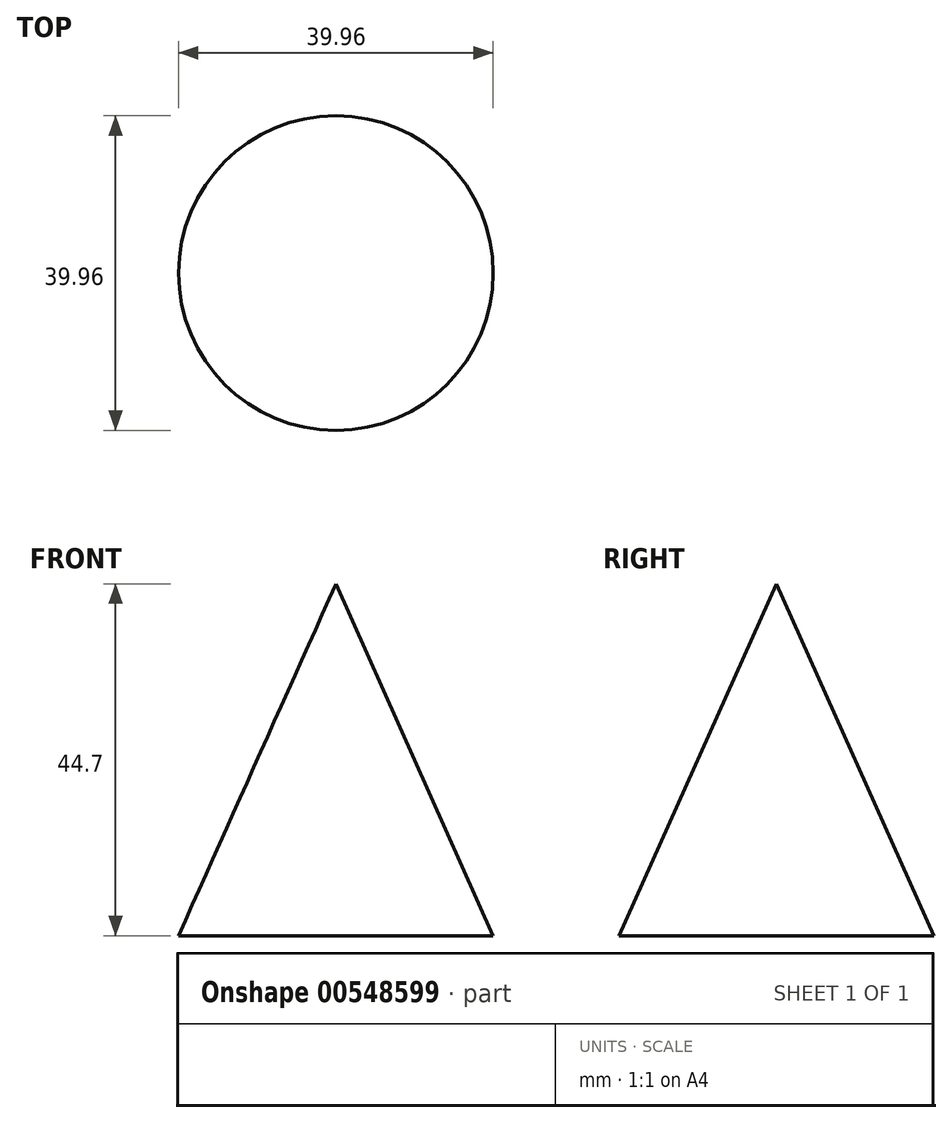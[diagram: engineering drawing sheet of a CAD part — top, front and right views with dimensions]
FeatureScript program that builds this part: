
annotation { "Feature Type Name" : "Feature", "Feature Type Description" : "" }
export const myFeature = defineFeature(function(context is Context, id is Id, definition is map)
    precondition{}
    {
        {
            var Q0;
            Q0=qCreatedBy(makeId("Front.planeOp"),FACE);
            var sketch = newSketch(context, id + "F0", { "sketchPlane" : qUnion([Q0])});
            skLineSegment(sketch, "E0", {"start": v(0, 44.7) * mm, "end": v(19.98, 0) * mm});
            skLineSegment(sketch, "E1", {"start": v(19.98, 0) * mm, "end": v(0, 0) * mm});
            skLineSegment(sketch, "E2", {"start": v(0, 0) * mm, "end": v(0, 44.7) * mm});
            skLineSegment(sketch, "E3", {"start": v(0, 58.62) * mm, "end": v(0, -7.4) * mm, "construction": true});
            skSolve(sketch);
        }
        {
            var Q0;
            Q0 = qSketchRegion(id + "F0", true);
            var Q1;
            Q1=sQuery(id+"F0.wireOp",EDGE,"E3");
            revolve(context, id + "F1", {"entities" : qUnion([Q0]), "axis" : qUnion([Q1]), "revolveType" : RevolveType.FULL});
        }
    });
